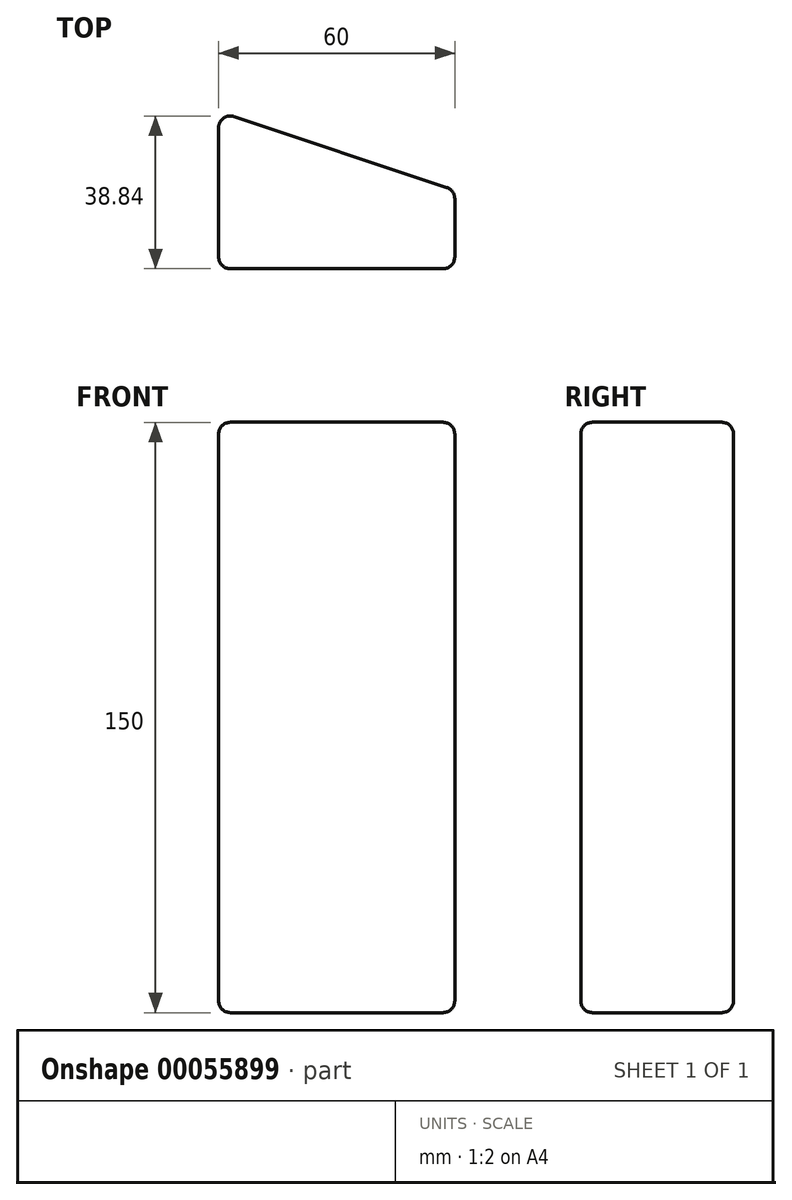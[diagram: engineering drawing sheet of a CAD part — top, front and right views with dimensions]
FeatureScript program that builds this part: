
annotation { "Feature Type Name" : "Feature", "Feature Type Description" : "" }
export const myFeature = defineFeature(function(context is Context, id is Id, definition is map)
    precondition{}
    {
        {
            var Q0;
            Q0=qCreatedBy(makeId("Right.planeOp"),FACE);
            var sketch = newSketch(context, id + "F0", { "sketchPlane" : qUnion([Q0])});
            skLineSegment(sketch, "E0.bottom", {"start": v(-83.19, 74.05) * mm, "end": v(-43.19, 74.05) * mm});
            skLineSegment(sketch, "E0.top", {"start": v(-83.19, -75.95) * mm, "end": v(-43.19, -75.95) * mm});
            skLineSegment(sketch, "E0.left", {"start": v(-83.19, 74.05) * mm, "end": v(-83.19, -75.95) * mm});
            skLineSegment(sketch, "E0.right", {"start": v(-43.19, 74.05) * mm, "end": v(-43.19, -75.95) * mm});
            skSolve(sketch);
        }
        {
            var Q0;
            Q0 = qSketchRegion(id + "F0", true);
            extrude(context, id + "F1", {"entities" : qUnion([Q0]), "depth" : 60 * mm});
        }
        {
            var Q0;
            Q0=makeQuery(id+"F1.opExtrude","CAP_EDGE",EDGE,{"disambiguationData":[OSD([sQuery(id+"F0.wireOp",EDGE,"E0.right")])],"isStart":false});
            chamfer(context, id + "F2", {"entities" : qUnion([Q0]), "chamferType" : ChamferType.TWO_OFFSETS, "width1" : 60 * mm, "oppositeDirection" : false, "width2" : 20 * mm, "tangentPropagation" : true});
        }
        {
            var Q0;
            {var subQ0=sQuery(id+"F0.wireOp",EDGE,"E0.right");Q0=makeQuery(id+"F2.opChamfer","BLEND_EDGE",EDGE,{"blendedFrom":[makeQuery(id+"F1.opExtrude","CAP_EDGE",EDGE,{"disambiguationData":[OSD([subQ0])],"isStart":false}),makeQuery(id+"F1.opExtrude","CAP_FACE",FACE,{"disambiguationData":[OSD([sQuery(id+"F0.wireOp",EDGE,"E0.bottom"),sQuery(id+"F0.wireOp",EDGE,"E0.top"),sQuery(id+"F0.wireOp",EDGE,"E0.left"),subQ0])],"isStart":false})],"blendedInto":[makeQuery(id+"F1.opExtrude","CAP_FACE",FACE,{"disambiguationData":[OSD([sQuery(id+"F0.wireOp",EDGE,"E0.bottom"),sQuery(id+"F0.wireOp",EDGE,"E0.top"),sQuery(id+"F0.wireOp",EDGE,"E0.left"),subQ0])],"isStart":false})]});}
            var Q1;
            Q1=makeQuery(id+"F2.opChamfer","BLEND_EDGE",EDGE,{"blendedFrom":[makeQuery(id+"F1.opExtrude","CAP_EDGE",EDGE,{"disambiguationData":[OSD([sQuery(id+"F0.wireOp",EDGE,"E0.right")])],"isStart":false}),makeQuery(id+"F1.opExtrude","SWEPT_FACE",FACE,{"disambiguationData":[OSD([sQuery(id+"F0.wireOp",EDGE,"E0.top")])]})],"blendedInto":[makeQuery(id+"F1.opExtrude","SWEPT_FACE",FACE,{"disambiguationData":[OSD([sQuery(id+"F0.wireOp",EDGE,"E0.top")])]})]});
            var Q2;
            {var subQ0=sQuery(id+"F0.wireOp",EDGE,"E0.right");Q2=makeQuery(id+"F2.opChamfer","BLEND_EDGE",EDGE,{"blendedFrom":[makeQuery(id+"F1.opExtrude","CAP_EDGE",EDGE,{"disambiguationData":[OSD([subQ0])],"isStart":false}),makeQuery(id+"F1.opExtrude","CAP_FACE",FACE,{"disambiguationData":[OSD([sQuery(id+"F0.wireOp",EDGE,"E0.bottom"),sQuery(id+"F0.wireOp",EDGE,"E0.top"),sQuery(id+"F0.wireOp",EDGE,"E0.left"),subQ0])],"isStart":true})],"blendedInto":[makeQuery(id+"F1.opExtrude","CAP_FACE",FACE,{"disambiguationData":[OSD([sQuery(id+"F0.wireOp",EDGE,"E0.bottom"),sQuery(id+"F0.wireOp",EDGE,"E0.top"),sQuery(id+"F0.wireOp",EDGE,"E0.left"),subQ0])],"isStart":true})]});}
            var Q3;
            Q3=makeQuery(id+"F1.opExtrude","CAP_EDGE",EDGE,{"disambiguationData":[OSD([sQuery(id+"F0.wireOp",EDGE,"E0.top")])],"isStart":true});
            var Q4;
            Q4=makeQuery(id+"F1.opExtrude","SWEPT_EDGE",EDGE,{"disambiguationData":[OSD([sQuery(id+"F0.wireOp",EDGE,"E0.top"),sQuery(id+"F0.wireOp",EDGE,"E0.left")])]});
            var Q5;
            Q5=makeQuery(id+"F1.opExtrude","CAP_EDGE",EDGE,{"disambiguationData":[OSD([sQuery(id+"F0.wireOp",EDGE,"E0.top")])],"isStart":false});
            var Q6;
            Q6=makeQuery(id+"F1.opExtrude","CAP_EDGE",EDGE,{"disambiguationData":[OSD([sQuery(id+"F0.wireOp",EDGE,"E0.left")])],"isStart":false});
            var Q7;
            Q7=makeQuery(id+"F1.opExtrude","CAP_EDGE",EDGE,{"disambiguationData":[OSD([sQuery(id+"F0.wireOp",EDGE,"E0.left")])],"isStart":true});
            var Q8;
            Q8=makeQuery(id+"F1.opExtrude","SWEPT_EDGE",EDGE,{"disambiguationData":[OSD([sQuery(id+"F0.wireOp",EDGE,"E0.bottom"),sQuery(id+"F0.wireOp",EDGE,"E0.left")])]});
            var Q9;
            Q9=makeQuery(id+"F1.opExtrude","SWEPT_FACE",FACE,{"disambiguationData":[OSD([sQuery(id+"F0.wireOp",EDGE,"E0.bottom")])]});
            var Q10;
            Q10=makeQuery(id+"F2.opChamfer","BLEND_EDGE",EDGE,{"blendedFrom":[makeQuery(id+"F1.opExtrude","CAP_EDGE",EDGE,{"disambiguationData":[OSD([sQuery(id+"F0.wireOp",EDGE,"E0.right")])],"isStart":false}),makeQuery(id+"F1.opExtrude","SWEPT_FACE",FACE,{"disambiguationData":[OSD([sQuery(id+"F0.wireOp",EDGE,"E0.bottom")])]})],"blendedInto":[makeQuery(id+"F1.opExtrude","SWEPT_FACE",FACE,{"disambiguationData":[OSD([sQuery(id+"F0.wireOp",EDGE,"E0.bottom")])]})]});
            var Q11;
            Q11=makeQuery(id+"F1.opExtrude","CAP_EDGE",EDGE,{"disambiguationData":[OSD([sQuery(id+"F0.wireOp",EDGE,"E0.bottom")])],"isStart":false});
            fillet(context, id + "F3", {"entities" : qUnion([Q0, Q1, Q2, Q3, Q4, Q5, Q6, Q7, Q8, Q9, Q10, Q11]), "radius" : 3 * mm, "tangentPropagation" : true, "allowEdgeOverflow" : false});
        }
    });
